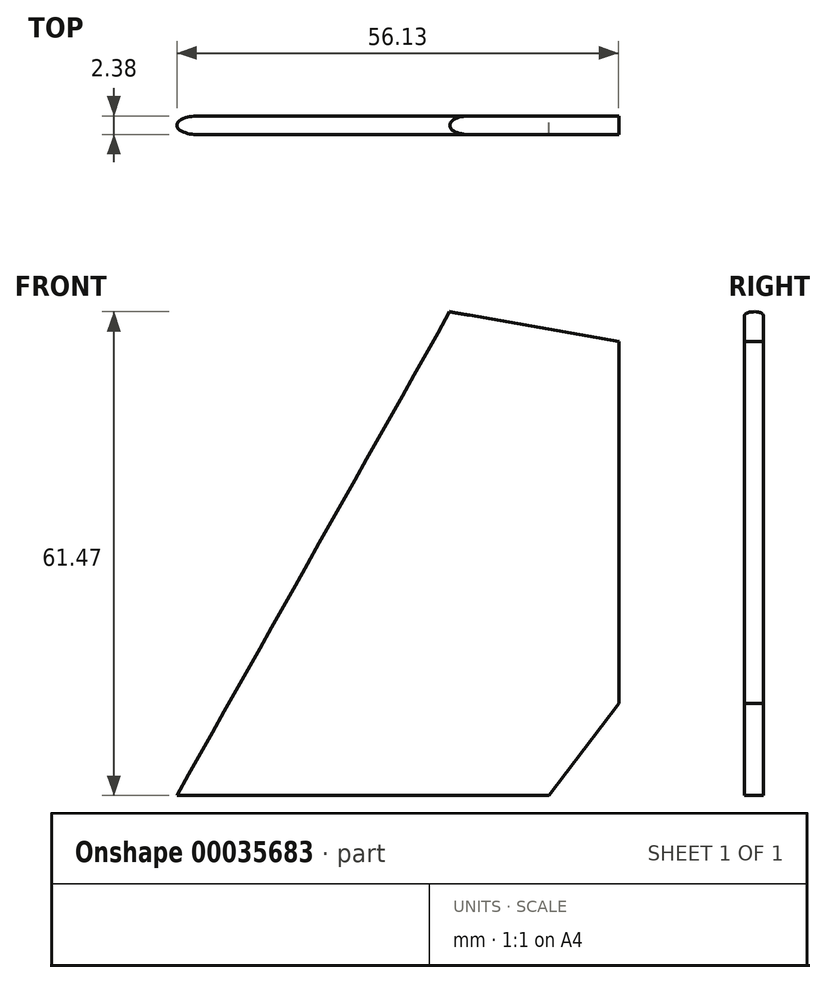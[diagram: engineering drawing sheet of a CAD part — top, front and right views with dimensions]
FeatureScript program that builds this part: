
annotation { "Feature Type Name" : "Feature", "Feature Type Description" : "" }
export const myFeature = defineFeature(function(context is Context, id is Id, definition is map)
    precondition{}
    {
        {
            var Q0;
            Q0=qCreatedBy(makeId("Front.planeOp"),FACE);
            var sketch = newSketch(context, id + "F0", { "sketchPlane" : qUnion([Q0])});
            skLineSegment(sketch, "E0", {"start": v(0, 0) * mm, "end": v(43.69, 77.47) * mm});
            skLineSegment(sketch, "E1", {"start": v(43.69, 77.47) * mm, "end": v(68.07, 73.15) * mm});
            skLineSegment(sketch, "E2", {"start": v(68.07, 73.15) * mm, "end": v(68.07, 11.68) * mm});
            skLineSegment(sketch, "E3", {"start": v(68.07, 11.68) * mm, "end": v(59.18, 0) * mm});
            skLineSegment(sketch, "E4", {"start": v(59.18, 0) * mm, "end": v(0, 0) * mm});
            skLineSegment(sketch, "E5", {"start": v(61.47, 64.82) * mm, "end": v(61.47, 11.68) * mm});
            skLineSegment(sketch, "E6", {"start": v(61.47, 11.68) * mm, "end": v(52.58, 0) * mm});
            skLineSegment(sketch, "E7", {"start": v(68.07, 11.68) * mm, "end": v(6.59, 11.68) * mm, "construction": true});
            skLineSegment(sketch, "E8", {"start": v(38.82, 68.83) * mm, "end": v(61.47, 64.82) * mm});
            skLineSegment(sketch, "E9", {"start": v(34.66, 61.47) * mm, "end": v(56.13, 57.67) * mm});
            skLineSegment(sketch, "E10", {"start": v(56.13, 57.67) * mm, "end": v(56.13, 11.68) * mm});
            skLineSegment(sketch, "E11", {"start": v(56.13, 11.68) * mm, "end": v(47.24, 0) * mm});
            skSolve(sketch);
        }
        {
            var Q0;
            {var subQ1=sQuery(id+"F0.wireOp",EDGE,"E9");Q0=makeQuery(id+"F0.imprint","IMPRINT",FACE,{"disambiguationData":[TD([[makeQuery(id+"F0.imprint","IMPRINT",EDGE,{"derivedFrom":subQ1}),-1.0]])]});}
            extrude(context, id + "F1", {"entities" : qUnion([Q0]), "depth" : 2.38 * mm, "symmetric" : true});
        }
        {
            var Q0;
            Q0=sQuery(id+"F0.wireOp",EDGE,"E0");
            var Q1;
            Q1=sQuery(id+"F0.wireOp",VERTEX,"E4.end");
            cPlane(context, id + "F2", {"entities" : qUnion([Q0, Q1]), "cplaneType" : CPlaneType.LINE_POINT, "offset" : 152.4 * mm, "width" : 152.4 * mm, "height" : 152.4 * mm});
        }
        {
            var Q0;
            Q0=qCreatedBy(id+"F2.planeOp",FACE);
            var sketch = newSketch(context, id + "F3", { "sketchPlane" : qUnion([Q0])});
            skLineSegment(sketch, "E12.1", {"start": v(2.38, 1.2) * mm, "end": v(20.57, 1.2) * mm});
            skLineSegment(sketch, "E12.2", {"start": v(2.38, -1.2) * mm, "end": v(20.57, -1.2) * mm});
            skLineSegment(sketch, "E13", {"start": v(20.57, 1.2) * mm, "end": v(20.57, 12.7) * mm});
            skLineSegment(sketch, "E14", {"start": v(20.57, 12.7) * mm, "end": v(-12.7, 12.7) * mm});
            skLineSegment(sketch, "E15", {"start": v(-12.7, 12.7) * mm, "end": v(-12.7, -12.7) * mm});
            skLineSegment(sketch, "E16", {"start": v(-12.7, -12.7) * mm, "end": v(20.57, -12.7) * mm});
            skLineSegment(sketch, "E17", {"start": v(20.57, -12.7) * mm, "end": v(20.57, -1.2) * mm});
            skLineSegment(sketch, "E18", {"start": v(2.38, 1.2) * mm, "end": v(2.38, -1.2) * mm, "construction": true});
            skLineSegment(sketch, "E19", {"start": v(0, 0) * mm, "end": v(2.38, 0) * mm});
            skLineSegment(sketch, "E20", {"start": v(2.38, 0) * mm, "end": v(0, 0) * mm, "construction": true});
            skEllipticalArc(sketch, "E21", {});
            skPoint(sketch, "E22.orphan", {"position": v(0, 1.2) * mm});
            const initialGuessF3  = {"E21": [0.00238125, 0, -1, 0, 0.00238125, 0.001190625, 4.71238898038469, 1.5707963267948966]};
            skSetInitialGuess(sketch, initialGuessF3);
            skSolve(sketch);
        }
        {
            var Q0;
            Q0 = qSketchRegion(id + "F3", true);
            extrude(context, id + "F4", {"entities" : qUnion([Q0]), "operationType" : NewBodyOperationType.REMOVE, "endBound" : BoundingType.THROUGH_ALL, "depth" : 25.4 * mm});
        }
    });
